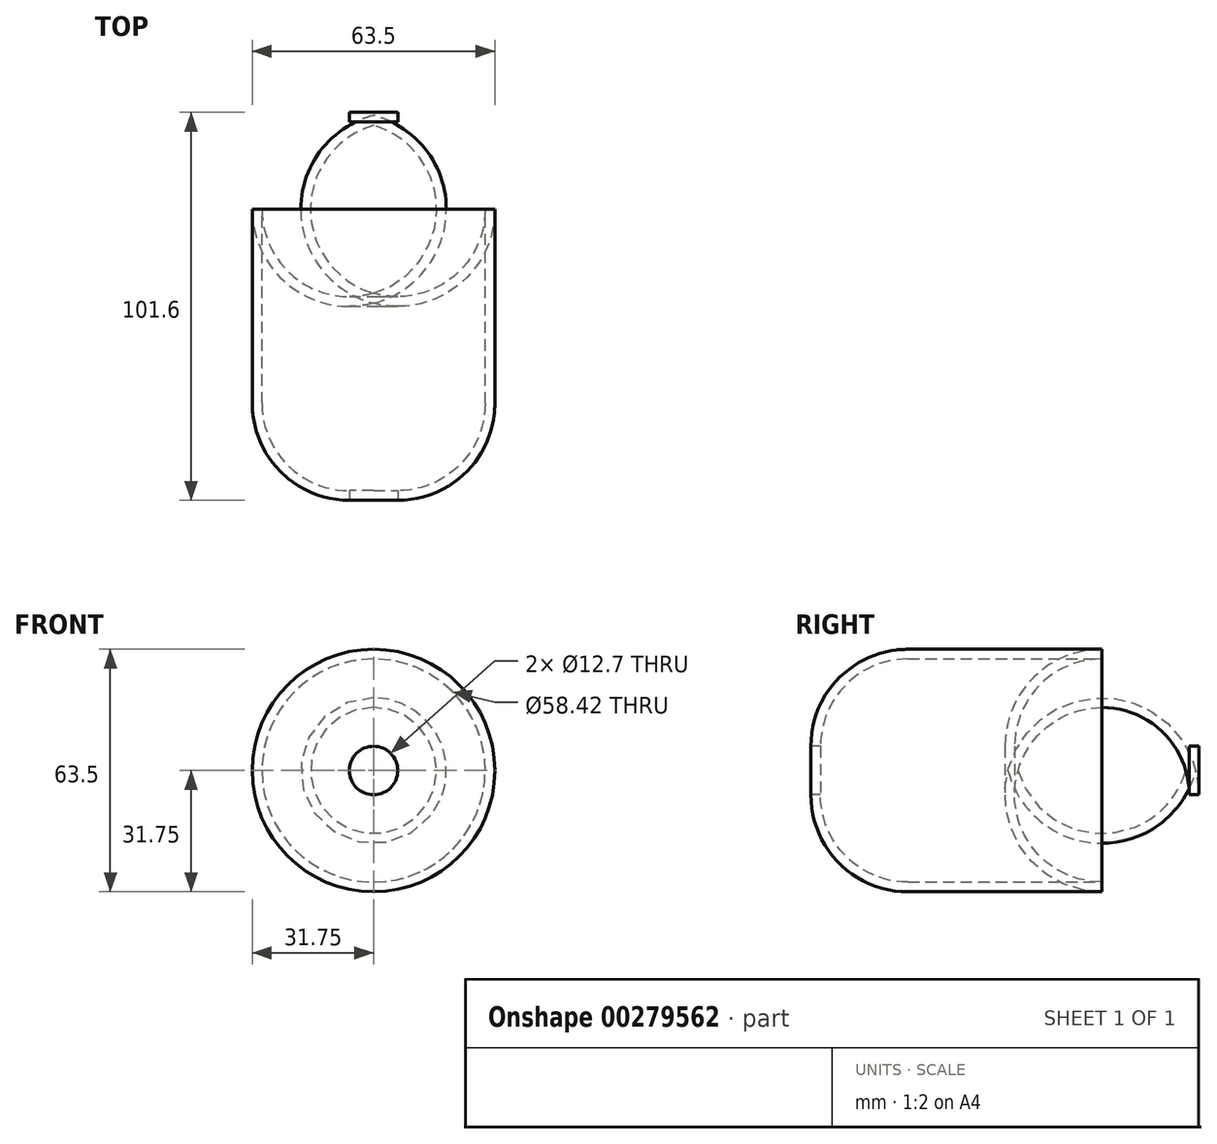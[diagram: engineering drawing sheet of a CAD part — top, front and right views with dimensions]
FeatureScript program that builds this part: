
annotation { "Feature Type Name" : "Feature", "Feature Type Description" : "" }
export const myFeature = defineFeature(function(context is Context, id is Id, definition is map)
    precondition{}
    {
        {
            var Q0;
            Q0=qCreatedBy(makeId("Front.planeOp"),FACE);
            var sketch = newSketch(context, id + "F0", { "sketchPlane" : qUnion([Q0])});
            skCircle(sketch, "E0", {"center": v(0, 0) * mm, "radius": 31.75 * mm});
            skSolve(sketch);
        }
        {
            var Q0;
            Q0=makeQuery(id+"F0.imprint","IMPRINT",FACE,{"disambiguationData":[TD([[makeQuery(id+"F0.imprint","IMPRINT",EDGE,{"derivedFrom":sQuery(id+"F0.wireOp",EDGE,"E0")}),1.0]])]});
            extrude(context, id + "F1", {"entities" : qUnion([Q0]), "endBound" : BoundingType.SYMMETRIC, "depth" : 101.6 * mm});
        }
        {
            var Q0;
            Q0=makeQuery(id+"F1.opExtrude","CAP_FACE",FACE,{"disambiguationData":[OSD([sQuery(id+"F0.wireOp",EDGE,"E0")])],"isStart":false});
            var Q1;
            Q1=makeQuery(id+"F1.opExtrude","CAP_FACE",FACE,{"disambiguationData":[OSD([sQuery(id+"F0.wireOp",EDGE,"E0")])],"isStart":true});
            fillet(context, id + "F2", {"entities" : qUnion([Q0, Q1]), "radius" : 25.4 * mm, "tangentPropagation" : true, "allowEdgeOverflow" : false});
        }
        {
            var Q0;
            Q0=makeQuery(id+"F1.opExtrude","CAP_FACE",FACE,{"disambiguationData":[OSD([sQuery(id+"F0.wireOp",EDGE,"E0")])],"isStart":false});
            var Q1;
            Q1=makeQuery(id+"F1.opExtrude","CAP_FACE",FACE,{"disambiguationData":[OSD([sQuery(id+"F0.wireOp",EDGE,"E0")])],"isStart":true});
            shell(context, id + "F3", {"entities" : qUnion([Q0, Q1]), "thickness" : 2.54 * mm});
        }
    });
